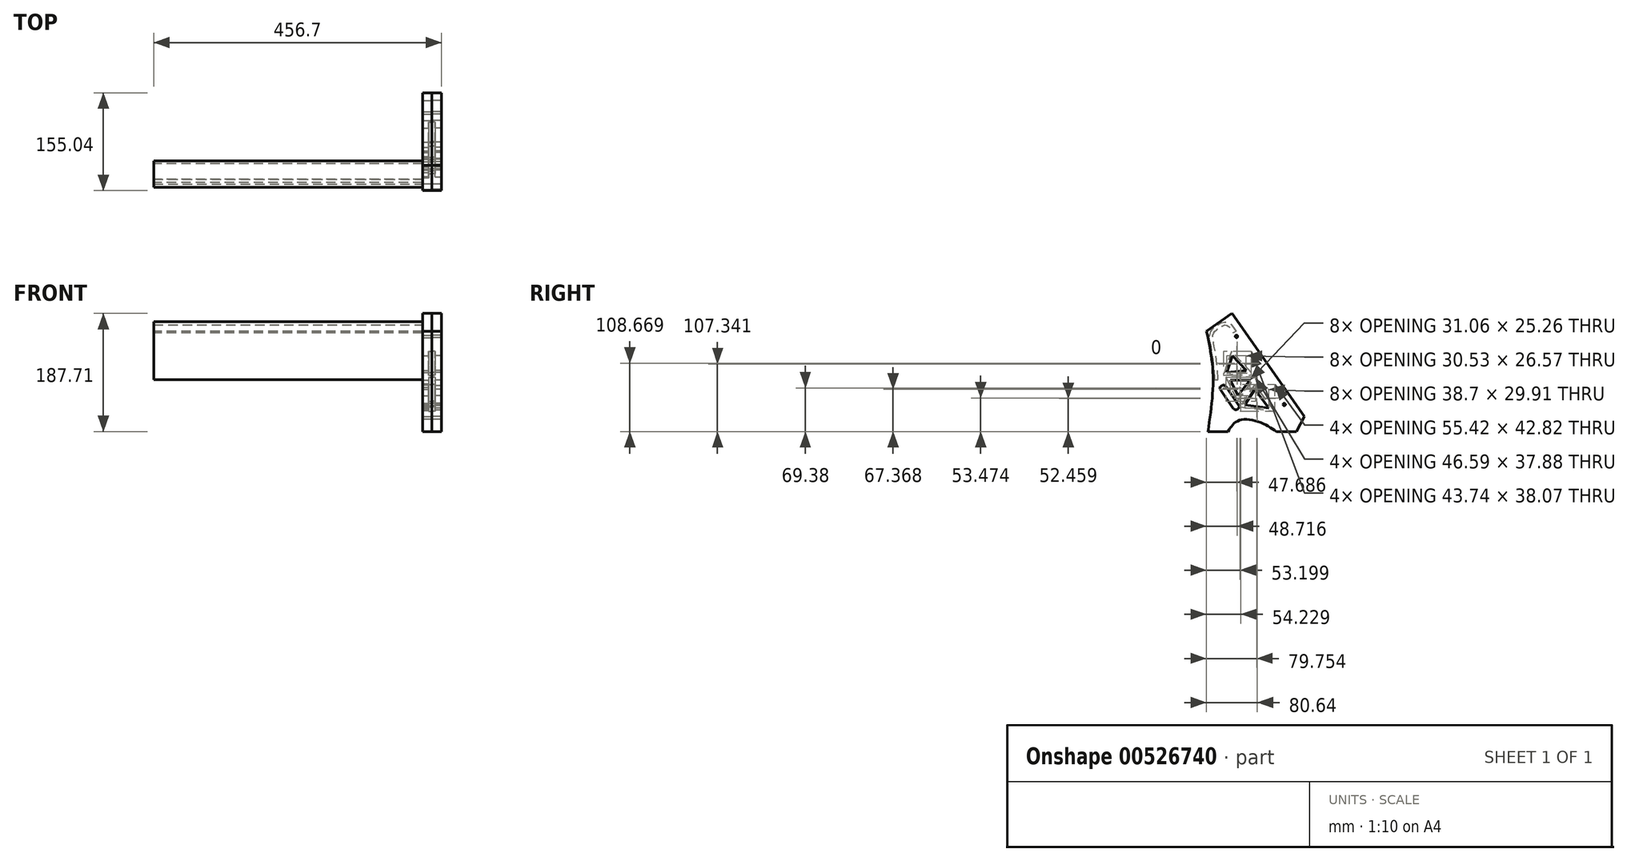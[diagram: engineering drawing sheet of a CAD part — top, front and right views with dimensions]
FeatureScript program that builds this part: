
annotation { "Feature Type Name" : "Feature", "Feature Type Description" : "" }
export const myFeature = defineFeature(function(context is Context, id is Id, definition is map)
    precondition{}
    {
        {
            var Q0;
            Q0=qCreatedBy(makeId("Right.planeOp"),FACE);
            var sketch = newSketch(context, id + "F0", { "sketchPlane" : qUnion([Q0])});
            skLineSegment(sketch, "E0", {"start": v(78.73, -61.03) * mm, "end": v(66.43, -84.9) * mm});
            skLineSegment(sketch, "E1", {"start": v(66.43, -84.9) * mm, "end": v(34.56, -84.9) * mm});
            skLineSegment(sketch, "E2", {"start": v(-35.98, 102.8) * mm, "end": v(-76.31, 74.53) * mm});
            skLineSegment(sketch, "E3", {"start": v(-35.98, 102.8) * mm, "end": v(78.73, -61.03) * mm});
            skLineSegment(sketch, "E4", {"start": v(-74.1, -84.9) * mm, "end": v(-42.24, -84.9) * mm});
            skFitSpline(sketch, "E5", {"points": [v(-42.24, -84.9) * mm, v(-32.6, -71.97) * mm, v(-16.64, -65.56) * mm, v(13.5, -72.27) * mm, v(34.56, -84.9) * mm], "startDerivative": vector(37.12, 66.33) * mm, "endDerivative": vector(75.27, -49.53) * mm});
            skFitSpline(sketch, "E6", {"points": [v(-76.31, 74.53) * mm, v(-65.92, 4.07) * mm, v(-74.1, -84.9) * mm], "startDerivative": vector(30.89, -144.9) * mm, "endDerivative": vector(-25.41, -173.45) * mm});
            skPoint(sketch, "E7", {"position": v(47, -41.88) * mm});
            skCircle(sketch, "E8", {"center": v(47, -41.88) * mm, "radius": 2 * mm});
            skLineSegment(sketch, "E9", {"start": v(47, -41.88) * mm, "end": v(-28.74, 66.23) * mm, "construction": true});
            skCircle(sketch, "E10", {"center": v(-28.74, 66.23) * mm, "radius": 2 * mm});
            skLineSegment(sketch, "E11", {"start": v(47, -41.88) * mm, "end": v(59.29, -33.27) * mm, "construction": true});
            skSolve(sketch);
        }
        {
            var Q0;
            Q0=qSketchRegion(id+"F0",true);
            extrude(context, id + "F1", {"entities" : qUnion([Q0]), "oppositeDirection" : true, "depth" : 15 * mm});
        }
        {
            var Q0;
            Q0=makeQuery(id+"F1.opExtrude","CAP_FACE",FACE,{"disambiguationData":[OSD([sQuery(id+"F0.wireOp",EDGE,"E0"),sQuery(id+"F0.wireOp",EDGE,"E1"),sQuery(id+"F0.wireOp",EDGE,"E2"),sQuery(id+"F0.wireOp",EDGE,"E3"),sQuery(id+"F0.wireOp",EDGE,"E4"),sQuery(id+"F0.wireOp",EDGE,"E5"),sQuery(id+"F0.wireOp",EDGE,"E6")])],"isStart":false});
            var sketch = newSketch(context, id + "F2", { "sketchPlane" : qUnion([Q0])});
            skLineSegment(sketch, "E12.bottom", {"start": v(48.52, -9.48) * mm, "end": v(56.7, -15.21) * mm});
            skLineSegment(sketch, "E12.top", {"start": v(22.7, -46.34) * mm, "end": v(30.9, -52.08) * mm});
            skLineSegment(sketch, "E12.left", {"start": v(48.52, -9.48) * mm, "end": v(22.7, -46.34) * mm});
            skLineSegment(sketch, "E12.right", {"start": v(56.7, -15.21) * mm, "end": v(30.9, -52.08) * mm});
            skSolve(sketch);
        }
        {
            var Q0;
            Q0=makeQuery(id+"F2.imprint","IMPRINT",FACE,{"disambiguationData":[TD([[makeQuery(id+"F2.imprint","IMPRINT",EDGE,{"derivedFrom":sQuery(id+"F2.wireOp",EDGE,"E12.bottom")}),-1.0]])]});
            extrude(context, id + "F3", {"entities" : qUnion([Q0]), "operationType" : NewBodyOperationType.REMOVE, "oppositeDirection" : true, "depth" : 10 * mm});
        }
        {
            var Q0;
            Q0=makeQuery(id+"F3.boolean.opBoolean","COPY",EDGE,{"derivedFrom":makeQuery(id+"F3.opExtrude","SWEPT_EDGE",EDGE,{"disambiguationData":[OSD([sQuery(id+"F2.wireOp",EDGE,"E12.bottom"),sQuery(id+"F2.wireOp",EDGE,"E12.left")])]})});
            var Q1;
            Q1=makeQuery(id+"F3.boolean.opBoolean","COPY",EDGE,{"derivedFrom":makeQuery(id+"F3.opExtrude","SWEPT_EDGE",EDGE,{"disambiguationData":[OSD([sQuery(id+"F2.wireOp",EDGE,"E12.bottom"),sQuery(id+"F2.wireOp",EDGE,"E12.right")])]})});
            var Q2;
            Q2=makeQuery(id+"F3.boolean.opBoolean","COPY",EDGE,{"derivedFrom":makeQuery(id+"F3.opExtrude","SWEPT_EDGE",EDGE,{"disambiguationData":[OSD([sQuery(id+"F2.wireOp",EDGE,"E12.top"),sQuery(id+"F2.wireOp",EDGE,"E12.right")])]})});
            var Q3;
            Q3=makeQuery(id+"F3.boolean.opBoolean","COPY",EDGE,{"derivedFrom":makeQuery(id+"F3.opExtrude","SWEPT_EDGE",EDGE,{"disambiguationData":[OSD([sQuery(id+"F2.wireOp",EDGE,"E12.top"),sQuery(id+"F2.wireOp",EDGE,"E12.left")])]})});
            fillet(context, id + "F4", {"entities" : qUnion([Q0, Q1, Q2, Q3]), "radius" : 5 * mm, "tangentPropagation" : true, "allowEdgeOverflow" : false});
        }
        {
            var Q0;
            Q0=makeQuery(id+"F1.opExtrude","CAP_FACE",FACE,{"disambiguationData":[OSD([sQuery(id+"F0.wireOp",EDGE,"E0"),sQuery(id+"F0.wireOp",EDGE,"E1"),sQuery(id+"F0.wireOp",EDGE,"E2"),sQuery(id+"F0.wireOp",EDGE,"E3"),sQuery(id+"F0.wireOp",EDGE,"E4"),sQuery(id+"F0.wireOp",EDGE,"E5"),sQuery(id+"F0.wireOp",EDGE,"E6")])],"isStart":true});
            var sketch = newSketch(context, id + "F5", { "sketchPlane" : qUnion([Q0])});
            skLineSegment(sketch, "E13", {"start": v(-36.7, 42.8) * mm, "end": v(-49.46, 4.73) * mm});
            skLineSegment(sketch, "E14", {"start": v(-49.46, 4.73) * mm, "end": v(-5.72, 8.98) * mm});
            skLineSegment(sketch, "E15", {"start": v(-5.72, 8.98) * mm, "end": v(-36.7, 42.8) * mm});
            skLineSegment(sketch, "E16", {"start": v(-34.98, 35.71) * mm, "end": v(-43.89, 9.15) * mm});
            skLineSegment(sketch, "E17", {"start": v(-43.89, 9.15) * mm, "end": v(-13.36, 12.12) * mm});
            skLineSegment(sketch, "E18", {"start": v(-13.36, 12.12) * mm, "end": v(-34.98, 35.71) * mm});
            skLineSegment(sketch, "E19", {"start": v(-45.38, 1.4) * mm, "end": v(-27.44, -36.48) * mm});
            skLineSegment(sketch, "E20", {"start": v(-27.44, -36.48) * mm, "end": v(1.22, 1.4) * mm});
            skLineSegment(sketch, "E21", {"start": v(1.22, 1.4) * mm, "end": v(-45.38, 1.4) * mm});
            skLineSegment(sketch, "E22", {"start": v(-38.64, -2.9) * mm, "end": v(-7.58, -2.9) * mm});
            skLineSegment(sketch, "E23", {"start": v(-7.58, -2.9) * mm, "end": v(-26.69, -28.16) * mm});
            skLineSegment(sketch, "E24", {"start": v(-26.69, -28.16) * mm, "end": v(-38.64, -2.9) * mm});
            skLineSegment(sketch, "E25", {"start": v(0.13, -10.02) * mm, "end": v(-23.38, -45.4) * mm});
            skLineSegment(sketch, "E26", {"start": v(-23.38, -45.4) * mm, "end": v(32.04, -52.85) * mm});
            skLineSegment(sketch, "E27", {"start": v(32.04, -52.85) * mm, "end": v(0.13, -10.02) * mm});
            skLineSegment(sketch, "E28", {"start": v(-15.9, -42.2) * mm, "end": v(0.51, -17.5) * mm});
            skLineSegment(sketch, "E29", {"start": v(0.51, -17.5) * mm, "end": v(22.8, -47.4) * mm});
            skLineSegment(sketch, "E30", {"start": v(22.8, -47.4) * mm, "end": v(-15.9, -42.2) * mm});
            skSolve(sketch);
        }
        {
            var Q0;
            Q0=makeQuery(id+"F5.imprint","IMPRINT",FACE,{"disambiguationData":[TD([[makeQuery(id+"F5.imprint","IMPRINT",EDGE,{"derivedFrom":sQuery(id+"F5.wireOp",EDGE,"E16")}),1.0]])]});
            extrude(context, id + "F6", {"entities" : qUnion([Q0]), "operationType" : NewBodyOperationType.REMOVE, "endBound" : BoundingType.UP_TO_NEXT, "oppositeDirection" : true, "depth" : 25 * mm});
        }
        {
            var Q0;
            Q0=makeQuery(id+"F5.imprint","IMPRINT",FACE,{"disambiguationData":[TD([[makeQuery(id+"F5.imprint","IMPRINT",EDGE,{"derivedFrom":sQuery(id+"F5.wireOp",EDGE,"E13")}),1.0]])]});
            extrude(context, id + "F7", {"entities" : qUnion([Q0]), "operationType" : NewBodyOperationType.REMOVE, "oppositeDirection" : true, "depth" : 5 * mm});
        }
        {
            var Q0;
            Q0=makeQuery(id+"F5.imprint","IMPRINT",FACE,{"disambiguationData":[TD([[makeQuery(id+"F5.imprint","IMPRINT",EDGE,{"derivedFrom":sQuery(id+"F5.wireOp",EDGE,"E22")}),-1.0]])]});
            extrude(context, id + "F8", {"entities" : qUnion([Q0]), "operationType" : NewBodyOperationType.REMOVE, "endBound" : BoundingType.UP_TO_NEXT, "oppositeDirection" : true, "depth" : 25 * mm});
        }
        {
            var Q0;
            Q0=makeQuery(id+"F5.imprint","IMPRINT",FACE,{"disambiguationData":[TD([[makeQuery(id+"F5.imprint","IMPRINT",EDGE,{"derivedFrom":sQuery(id+"F5.wireOp",EDGE,"E19")}),1.0]])]});
            extrude(context, id + "F9", {"entities" : qUnion([Q0]), "operationType" : NewBodyOperationType.REMOVE, "oppositeDirection" : true, "depth" : 5 * mm});
        }
        {
            var Q0;
            Q0=makeQuery(id+"F5.imprint","IMPRINT",FACE,{"disambiguationData":[TD([[makeQuery(id+"F5.imprint","IMPRINT",EDGE,{"derivedFrom":sQuery(id+"F5.wireOp",EDGE,"E28")}),-1.0]])]});
            extrude(context, id + "F10", {"entities" : qUnion([Q0]), "operationType" : NewBodyOperationType.REMOVE, "endBound" : BoundingType.UP_TO_NEXT, "oppositeDirection" : true, "depth" : 25 * mm});
        }
        {
            var Q0;
            Q0=makeQuery(id+"F5.imprint","IMPRINT",FACE,{"disambiguationData":[TD([[makeQuery(id+"F5.imprint","IMPRINT",EDGE,{"derivedFrom":sQuery(id+"F5.wireOp",EDGE,"E25")}),1.0]])]});
            extrude(context, id + "F11", {"entities" : qUnion([Q0]), "operationType" : NewBodyOperationType.REMOVE, "oppositeDirection" : true, "depth" : 5 * mm});
        }
        {
            var Q0;
            Q0=makeQuery(id+"F1.opExtrude","CAP_FACE",FACE,{"disambiguationData":[OSD([sQuery(id+"F0.wireOp",EDGE,"E0"),sQuery(id+"F0.wireOp",EDGE,"E1"),sQuery(id+"F0.wireOp",EDGE,"E2"),sQuery(id+"F0.wireOp",EDGE,"E3"),sQuery(id+"F0.wireOp",EDGE,"E4"),sQuery(id+"F0.wireOp",EDGE,"E5"),sQuery(id+"F0.wireOp",EDGE,"E6"),sQuery(id+"F0.wireOp",EDGE,"E8"),sQuery(id+"F0.wireOp",EDGE,"E10")])],"isStart":false});
            var sketch = newSketch(context, id + "F12", { "sketchPlane" : qUnion([Q0])});
            skFitSpline(sketch, "E31", {"points": [v(60.6, -2.7) * mm, v(61.95, 20.43) * mm, v(65.38, 43.8) * mm, v(67.74, 57.6) * mm, v(68.1, 70.07) * mm, v(60.85, 79.49) * mm, v(45.29, 86.54) * mm, v(31.78, 72.65) * mm], "startDerivative": vector(-3.94, 91.78) * mm, "endDerivative": vector(-94.96, -155.93) * mm});
            skSolve(sketch);
        }
        {
            var Q0;
            Q0=qCreatedBy(makeId("Top.planeOp"),FACE);
            var sketch = newSketch(context, id + "F13", { "sketchPlane" : qUnion([Q0])});
            skLineSegment(sketch, "E32.bottom", {"start": v(-15, -63.27) * mm, "end": v(-441.7, -63.27) * mm});
            skLineSegment(sketch, "E32.top", {"start": v(-15, -58.27) * mm, "end": v(-441.7, -58.27) * mm});
            skLineSegment(sketch, "E32.left", {"start": v(-15, -63.27) * mm, "end": v(-15, -58.27) * mm});
            skLineSegment(sketch, "E32.right", {"start": v(-441.7, -63.27) * mm, "end": v(-441.7, -58.27) * mm});
            skSolve(sketch);
        }
        {
            var Q0;
            Q0=makeQuery(id+"F13.imprint","IMPRINT",FACE,{"disambiguationData":[TD([[makeQuery(id+"F13.imprint","IMPRINT",EDGE,{"derivedFrom":sQuery(id+"F13.wireOp",EDGE,"E32.bottom")}),-1.0]])]});
            var Q1;
            Q1=sQuery(id+"F12.wireOp",EDGE,"E31");
            sweep(context, id + "F14", {"profiles" : qUnion([Q0]), "path" : qUnion([Q1])});
        }
        {
            var Q0;
            Q0=makeQuery(id+"F1.opExtrude","SWEPT_BODY",BODY,{"disambiguationData":[OSD([sQuery(id+"F0.wireOp",EDGE,"E0"),sQuery(id+"F0.wireOp",EDGE,"E1"),sQuery(id+"F0.wireOp",EDGE,"E2"),sQuery(id+"F0.wireOp",EDGE,"E3"),sQuery(id+"F0.wireOp",EDGE,"E4"),sQuery(id+"F0.wireOp",EDGE,"E5"),sQuery(id+"F0.wireOp",EDGE,"E6"),sQuery(id+"F0.wireOp",EDGE,"E8"),sQuery(id+"F0.wireOp",EDGE,"E10")])]});
            var Q1;
            Q1=qCreatedBy(makeId("Right.planeOp"),FACE);
            mirror(context, id + "F15", {"entities" : qUnion([Q0]), "mirrorPlane" : qUnion([Q1])});
        }
    });
